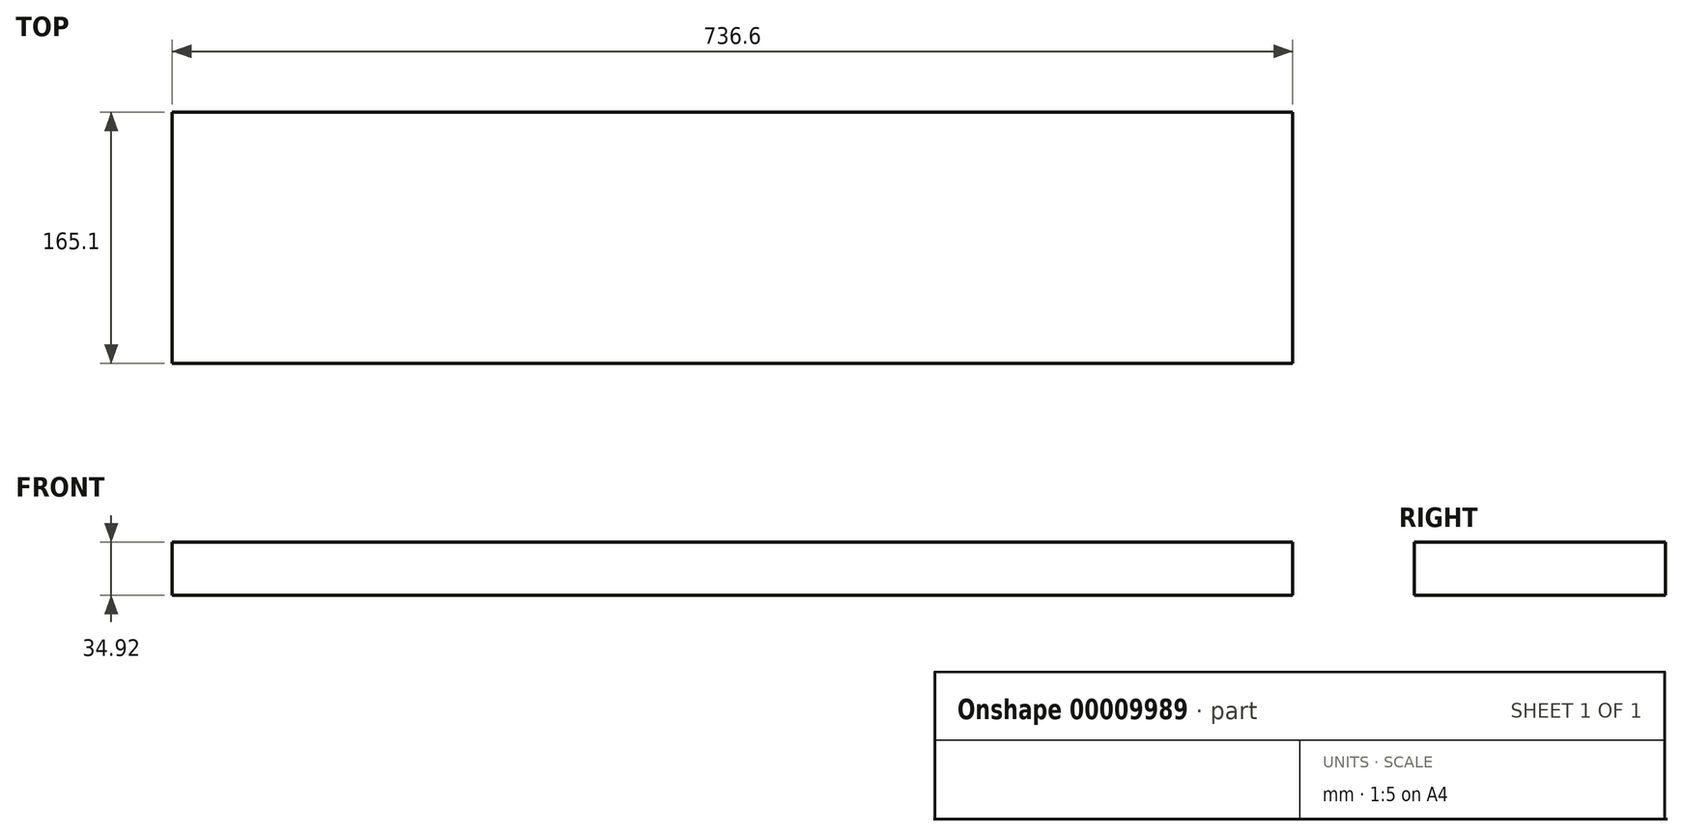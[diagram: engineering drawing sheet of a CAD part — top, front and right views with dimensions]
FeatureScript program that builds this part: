
annotation { "Feature Type Name" : "Feature", "Feature Type Description" : "" }
export const myFeature = defineFeature(function(context is Context, id is Id, definition is map)
    precondition{}
    {
        {
            var Q0;
            Q0=qCreatedBy(makeId("Top.planeOp"),FACE);
            var sketch = newSketch(context, id + "F0", { "sketchPlane" : qUnion([Q0])});
            skLineSegment(sketch, "E0.rect.bottom", {"start": v(-368.3, 82.55) * mm, "end": v(368.3, 82.55) * mm});
            skLineSegment(sketch, "E0.rect.top", {"start": v(-368.3, -82.55) * mm, "end": v(368.3, -82.55) * mm});
            skLineSegment(sketch, "E0.rect.left", {"start": v(-368.3, 82.55) * mm, "end": v(-368.3, -82.55) * mm});
            skLineSegment(sketch, "E0.rect.right", {"start": v(368.3, 82.55) * mm, "end": v(368.3, -82.55) * mm});
            skPoint(sketch, "E0.rect.middle", {"position": v(0, 0) * mm});
            skSolve(sketch);
        }
        {
            var Q0;
            Q0 = qSketchRegion(id + "F0", true);
            extrude(context, id + "F1", {"entities" : qUnion([Q0]), "depth" : 34.92 * mm});
        }
    });
